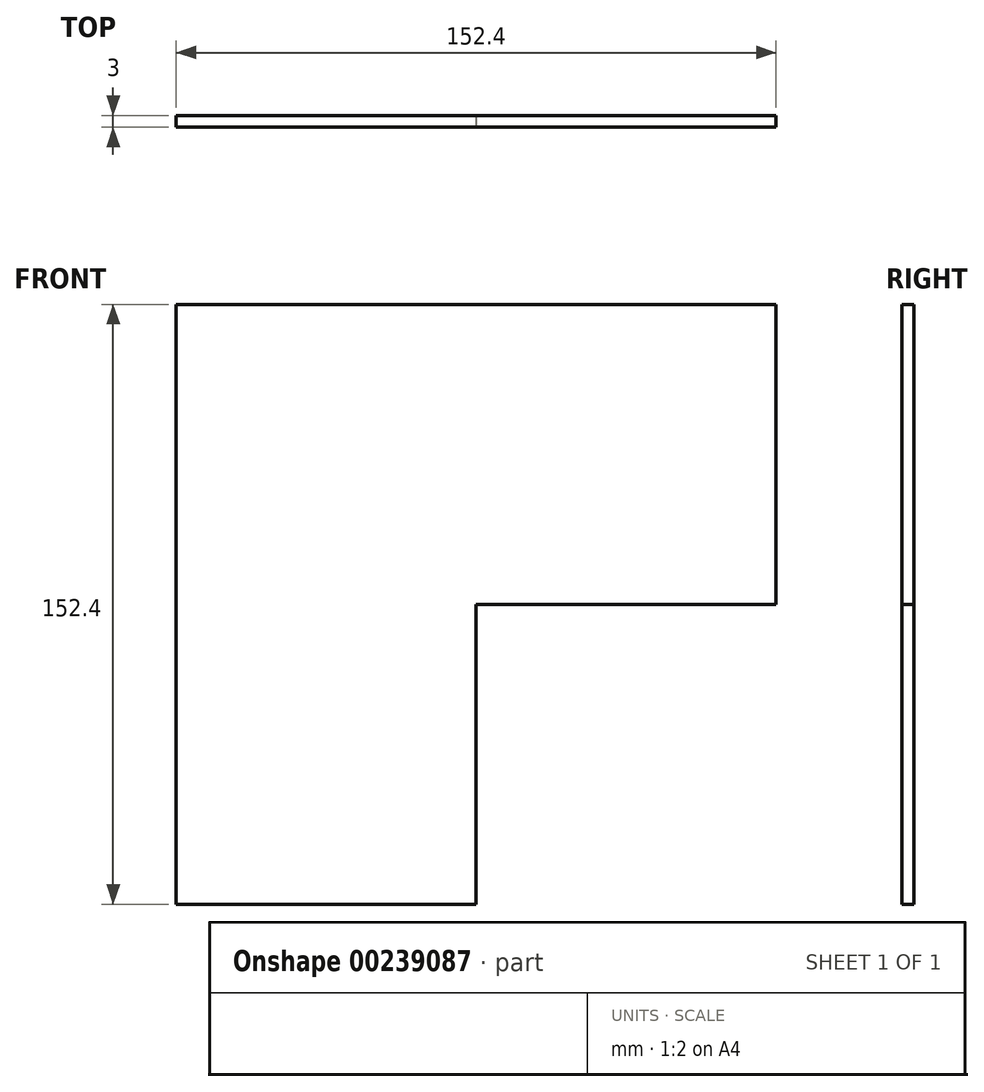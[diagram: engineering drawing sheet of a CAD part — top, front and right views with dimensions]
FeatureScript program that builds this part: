
annotation { "Feature Type Name" : "Feature", "Feature Type Description" : "" }
export const myFeature = defineFeature(function(context is Context, id is Id, definition is map)
    precondition{}
    {
        {
            assignVariable(context, id + "F0", {"name" : "v", "anyValue" : 3});
        }
        {
            var Q0;
            Q0=qCreatedBy(makeId("Front.planeOp"),FACE);
            var sketch = newSketch(context, id + "F1", { "sketchPlane" : qUnion([Q0])});
            skLineSegment(sketch, "E0.bottom", {"start": v(-76.2, 76.2) * mm, "end": v(76.2, 76.2) * mm});
            skLineSegment(sketch, "E0.top", {"start": v(-76.2, -76.2) * mm, "end": v(76.2, -76.2) * mm});
            skLineSegment(sketch, "E0.left", {"start": v(-76.2, 76.2) * mm, "end": v(-76.2, -76.2) * mm});
            skLineSegment(sketch, "E0.right", {"start": v(76.2, 76.2) * mm, "end": v(76.2, -76.2) * mm});
            skPoint(sketch, "E0.middle", {"position": v(0, 0) * mm});
            skSolve(sketch);
        }
        {
            var Q0;
            Q0 = qSketchRegion(id + "F1", true);
            extrude(context, id + "F2", {"entities" : qUnion([Q0]), "depth" : (getVariable(context, 'v')) * mm});
        }
        {
            var Q0;
            Q0=makeQuery(id+"F2.opExtrude","CAP_FACE",FACE,{"disambiguationData":[OSD([sQuery(id+"F1.wireOp",EDGE,"E0.bottom"),sQuery(id+"F1.wireOp",EDGE,"E0.top"),sQuery(id+"F1.wireOp",EDGE,"E0.left"),sQuery(id+"F1.wireOp",EDGE,"E0.right")])],"isStart":false});
            var sketch = newSketch(context, id + "F3", { "sketchPlane" : qUnion([Q0])});
            skLineSegment(sketch, "E1.bottom", {"start": v(0, 0) * mm, "end": v(76.2, 0) * mm});
            skLineSegment(sketch, "E1.top", {"start": v(0, -76.2) * mm, "end": v(76.2, -76.2) * mm});
            skLineSegment(sketch, "E1.left", {"start": v(0, 0) * mm, "end": v(0, -76.2) * mm});
            skLineSegment(sketch, "E1.right", {"start": v(76.2, 0) * mm, "end": v(76.2, -76.2) * mm});
            skSolve(sketch);
        }
        {
            var Q0;
            Q0 = qSketchRegion(id + "F3", true);
            extrude(context, id + "F4", {"entities" : qUnion([Q0]), "operationType" : NewBodyOperationType.REMOVE, "endBound" : BoundingType.THROUGH_ALL, "oppositeDirection" : true, "depth" : 25.4 * mm});
        }
    });
